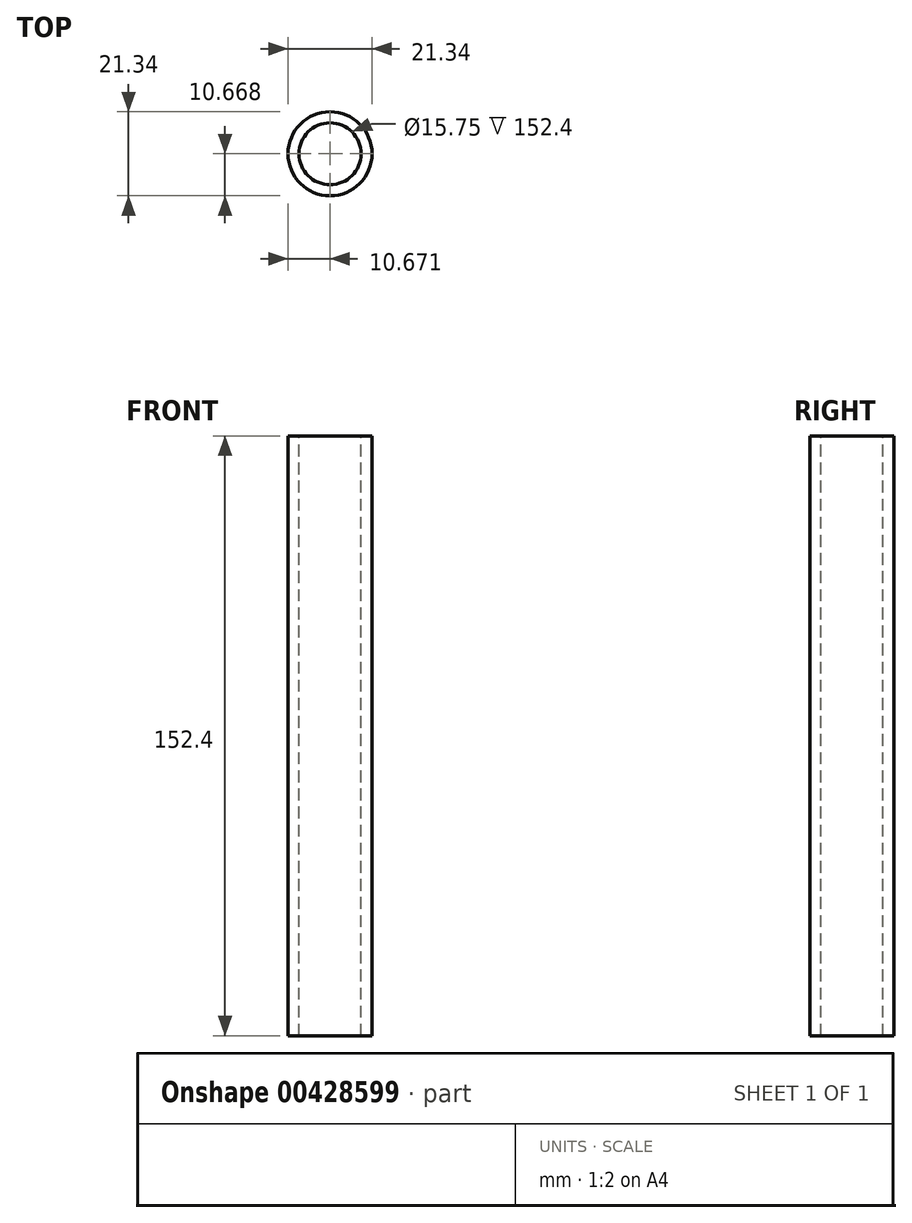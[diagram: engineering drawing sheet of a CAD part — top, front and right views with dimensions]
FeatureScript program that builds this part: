
annotation { "Feature Type Name" : "Feature", "Feature Type Description" : "" }
export const myFeature = defineFeature(function(context is Context, id is Id, definition is map)
    precondition{}
    {
        {
            var Q0;
            Q0=qCreatedBy(makeId("Top.planeOp"),FACE);
            var sketch = newSketch(context, id + "F0", { "sketchPlane" : qUnion([Q0])});
            skCircle(sketch, "E0", {"center": v(72.06, 47.03) * mm, "radius": 10.67 * mm});
            skSolve(sketch);
        }
        {
            var Q0;
            Q0=makeQuery(id+"F0.imprint","IMPRINT",FACE,{"disambiguationData":[TD([[makeQuery(id+"F0.imprint","IMPRINT",EDGE,{"derivedFrom":sQuery(id+"F0.wireOp",EDGE,"E0")}),1.0]])]});
            var sketch = newSketch(context, id + "F1", { "sketchPlane" : qUnion([Q0])});
            skCircle(sketch, "E1", {"center": v(72.06, 47.03) * mm, "radius": 7.87 * mm});
            skSolve(sketch);
        }
        {
            var Q0;
            Q0=makeQuery(id+"F1.imprint","IMPRINT",FACE,{"disambiguationData":[TD([[makeQuery(id+"F1.imprint","IMPRINT",EDGE,{"derivedFrom":sQuery(id+"F1.wireOp",EDGE,"E1")}),-1.0]])]});
            extrude(context, id + "F2", {"entities" : qUnion([Q0]), "oppositeDirection" : true, "depth" : 152.4 * mm});
        }
    });
